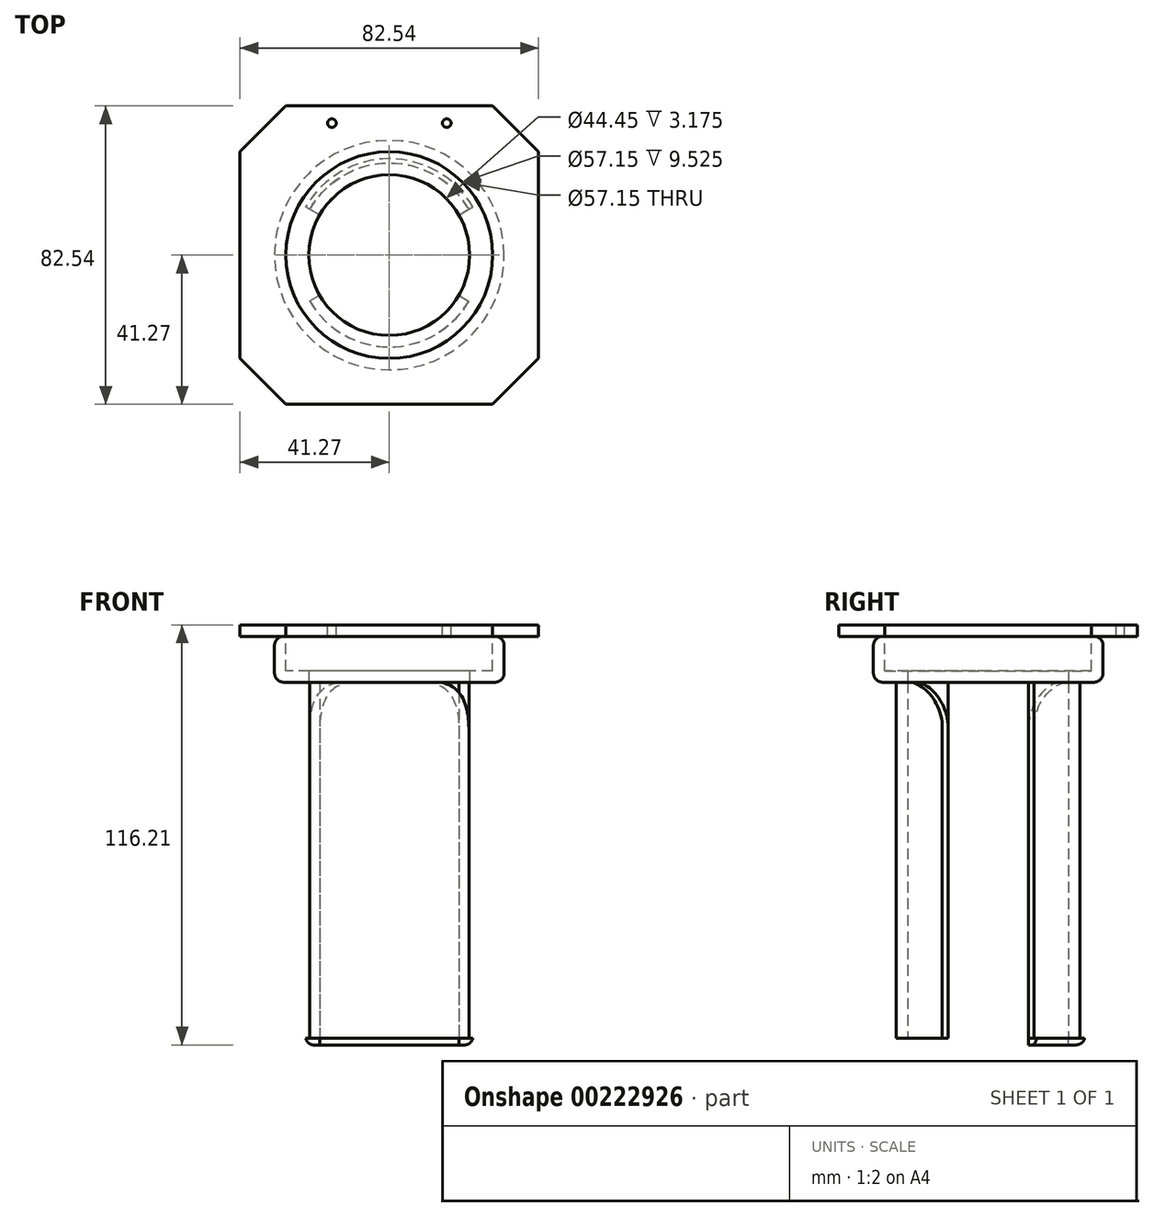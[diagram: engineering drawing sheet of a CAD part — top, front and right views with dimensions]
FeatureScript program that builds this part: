
annotation { "Feature Type Name" : "Feature", "Feature Type Description" : "" }
export const myFeature = defineFeature(function(context is Context, id is Id, definition is map)
    precondition{}
    {
        {
            var Q0;
            Q0=qCreatedBy(makeId("Top.planeOp"),FACE);
            var sketch = newSketch(context, id + "F0", { "sketchPlane" : qUnion([Q0])});
            skCircle(sketch, "E0", {"center": v(0, 0) * mm, "radius": 25.4 * mm});
            skCircle(sketch, "E1", {"center": v(0, 0) * mm, "radius": 22.23 * mm});
            skLineSegment(sketch, "E2", {"start": v(-12.7, 22) * mm, "end": v(12.7, -22) * mm});
            skLineSegment(sketch, "E3", {"start": v(12.7, 22) * mm, "end": v(-12.7, -22) * mm});
            skSolve(sketch);
        }
        {
            var Q0;
            {var subQ0=sQuery(id+"F0.wireOp",EDGE,"E2");var subQ1=sQuery(id+"F0.wireOp",EDGE,"E0");var subQ2=makeQuery(id+"F0.imprint","INTERSECT",VERTEX,{"disambiguationData":[OD(0.0)],"derivedFrom":[subQ1,subQ0]});Q0=makeQuery(id+"F0.imprint","IMPRINT",FACE,{"disambiguationData":[TD([[makeQuery(id+"F0.imprint","IMPRINT",EDGE,{"disambiguationData":[TD([[subQ2,-1.0]])],"derivedFrom":subQ1}),1.0]])]});}
            var Q1;
            {var subQ0=sQuery(id+"F0.wireOp",EDGE,"E2");var subQ1=sQuery(id+"F0.wireOp",EDGE,"E0");var subQ2=makeQuery(id+"F0.imprint","INTERSECT",VERTEX,{"disambiguationData":[OD(1.0)],"derivedFrom":[subQ1,subQ0]});Q1=makeQuery(id+"F0.imprint","IMPRINT",FACE,{"disambiguationData":[TD([[makeQuery(id+"F0.imprint","IMPRINT",EDGE,{"disambiguationData":[TD([[subQ2,-1.0]])],"derivedFrom":subQ1}),1.0]])]});}
            extrude(context, id + "F1", {"entities" : qUnion([Q0, Q1]), "depth" : 98.42 * mm});
        }
        {
            var Q0;
            {var subQ0=sQuery(id+"F0.wireOp",EDGE,"E3");var subQ1=sQuery(id+"F0.wireOp",EDGE,"E0");var subQ2=makeQuery(id+"F0.imprint","INTERSECT",VERTEX,{"disambiguationData":[OD(1.0)],"derivedFrom":[subQ1,subQ0]});var subQ3=sQuery(id+"F0.wireOp",EDGE,"E1");var subQ5=sQuery(id+"F0.wireOp",EDGE,"E2");var subQ6=makeQuery(id+"F0.imprint","INTERSECT",VERTEX,{"disambiguationData":[OD(0.0)],"derivedFrom":[subQ1,subQ5]});var subQ7=makeQuery(id+"F0.imprint","INTERSECT",VERTEX,{"disambiguationData":[OD(0.0)],"derivedFrom":[subQ3,subQ5]});Q0=makeQuery(id+"F1.opExtrude","CAP_FACE",FACE,{"disambiguationData":[OSD([subQ1,subQ3,subQ5,subQ0]),TDD([makeQuery(id+"F0.imprint","IMPRINT",EDGE,{"disambiguationData":[TD([[subQ6,-1.0]])],"derivedFrom":subQ1}),makeQuery(id+"F0.imprint","IMPRINT",EDGE,{"disambiguationData":[TD([[subQ7,-1.0]])],"derivedFrom":subQ3}),makeQuery(id+"F0.imprint","IMPRINT",EDGE,{"disambiguationData":[TD([[subQ6,-1.0]])],"derivedFrom":subQ5}),makeQuery(id+"F0.imprint","IMPRINT",EDGE,{"disambiguationData":[TD([[subQ2,1.0]])],"derivedFrom":subQ0})])],"isStart":true});}
            var sketch = newSketch(context, id + "F2", { "sketchPlane" : qUnion([Q0])});
            skCircle(sketch, "E4", {"center": v(0, 0) * mm, "radius": 26.67 * mm});
            skCircle(sketch, "E5", {"center": v(0, 0) * mm, "radius": 22.23 * mm});
            skLineSegment(sketch, "E6", {"start": v(11.11, -19.25) * mm, "end": v(13.34, -23.1) * mm});
            skLineSegment(sketch, "E7", {"start": v(-11.11, -19.25) * mm, "end": v(-13.34, -23.1) * mm});
            skLineSegment(sketch, "E8", {"start": v(-11.11, 19.25) * mm, "end": v(-13.33, 23.1) * mm});
            skLineSegment(sketch, "E9", {"start": v(11.11, 19.25) * mm, "end": v(13.33, 23.1) * mm});
            skSolve(sketch);
        }
        {
            var Q0;
            {var subQ5=sQuery(id+"F0.wireOp",EDGE,"E0");var subQ6=makeQuery(id+"F1.opExtrude","CAP_EDGE",EDGE,{"disambiguationData":[OSD([subQ5]),TDD([makeQuery(id+"F0.imprint","IMPRINT",EDGE,{"disambiguationData":[TD([[makeQuery(id+"F0.imprint","INTERSECT",VERTEX,{"disambiguationData":[OD(0.0)],"derivedFrom":[subQ5,sQuery(id+"F0.wireOp",EDGE,"E2")]}),-1.0]])],"derivedFrom":subQ5})])],"isStart":true});Q0=makeQuery(id+"F2.imprint","IMPRINT",FACE,{"disambiguationData":[TD([[makeQuery(id+"F2.imprint","IMPRINT",EDGE,{"derivedFrom":subQ6}),1.0]])]});}
            var Q1;
            {var subQ0=sQuery(id+"F2.wireOp",EDGE,"E6");Q1=makeQuery(id+"F2.imprint","IMPRINT",FACE,{"disambiguationData":[TD([[makeQuery(id+"F2.imprint","IMPRINT",EDGE,{"derivedFrom":subQ0}),1.0]])]});}
            var Q2;
            {var subQ5=sQuery(id+"F0.wireOp",EDGE,"E0");var subQ6=makeQuery(id+"F1.opExtrude","CAP_EDGE",EDGE,{"disambiguationData":[OSD([subQ5]),TDD([makeQuery(id+"F0.imprint","IMPRINT",EDGE,{"disambiguationData":[TD([[makeQuery(id+"F0.imprint","INTERSECT",VERTEX,{"disambiguationData":[OD(0.0)],"derivedFrom":[subQ5,sQuery(id+"F0.wireOp",EDGE,"E2")]}),-1.0]])],"derivedFrom":subQ5})])],"isStart":true});Q2=makeQuery(id+"F2.imprint","IMPRINT",FACE,{"disambiguationData":[TD([[makeQuery(id+"F2.imprint","IMPRINT",EDGE,{"derivedFrom":subQ6}),-1.0]])]});}
            extrude(context, id + "F3", {"entities" : qUnion([Q0, Q1, Q2]), "depth" : 1.9 * mm});
        }
        {
            var Q0;
            {var subQ0=sQuery(id+"F0.wireOp",EDGE,"E3");var subQ1=sQuery(id+"F0.wireOp",EDGE,"E0");var subQ2=makeQuery(id+"F0.imprint","INTERSECT",VERTEX,{"disambiguationData":[OD(1.0)],"derivedFrom":[subQ1,subQ0]});var subQ3=sQuery(id+"F0.wireOp",EDGE,"E1");var subQ5=sQuery(id+"F0.wireOp",EDGE,"E2");var subQ6=makeQuery(id+"F0.imprint","INTERSECT",VERTEX,{"disambiguationData":[OD(0.0)],"derivedFrom":[subQ1,subQ5]});var subQ7=makeQuery(id+"F0.imprint","INTERSECT",VERTEX,{"disambiguationData":[OD(0.0)],"derivedFrom":[subQ3,subQ5]});Q0=makeQuery(id+"F1.opExtrude","CAP_FACE",FACE,{"disambiguationData":[OSD([subQ1,subQ3,subQ5,subQ0]),TDD([makeQuery(id+"F0.imprint","IMPRINT",EDGE,{"disambiguationData":[TD([[subQ6,-1.0]])],"derivedFrom":subQ1}),makeQuery(id+"F0.imprint","IMPRINT",EDGE,{"disambiguationData":[TD([[subQ7,-1.0]])],"derivedFrom":subQ3}),makeQuery(id+"F0.imprint","IMPRINT",EDGE,{"disambiguationData":[TD([[subQ6,-1.0]])],"derivedFrom":subQ5}),makeQuery(id+"F0.imprint","IMPRINT",EDGE,{"disambiguationData":[TD([[subQ2,1.0]])],"derivedFrom":subQ0})])],"isStart":false});}
            var sketch = newSketch(context, id + "F4", { "sketchPlane" : qUnion([Q0])});
            skCircle(sketch, "E10", {"center": v(0, 0) * mm, "radius": 31.75 * mm});
            skSolve(sketch);
        }
        {
            var Q0;
            Q0 = qSketchRegion(id + "F4", true);
            extrude(context, id + "F5", {"entities" : qUnion([Q0]), "depth" : 12.7 * mm});
        }
        {
            var Q0;
            Q0=makeQuery(id+"F5.opExtrude","CAP_FACE",FACE,{"disambiguationData":[OSD([sQuery(id+"F4.wireOp",EDGE,"E10")])],"isStart":false});
            var sketch = newSketch(context, id + "F6", { "sketchPlane" : qUnion([Q0])});
            skLineSegment(sketch, "E11.bottom", {"start": v(41.27, 41.28) * mm, "end": v(-41.28, 41.28) * mm});
            skLineSegment(sketch, "E11.top", {"start": v(41.28, -41.28) * mm, "end": v(-41.27, -41.28) * mm});
            skLineSegment(sketch, "E11.left", {"start": v(41.27, 41.28) * mm, "end": v(41.28, -41.28) * mm});
            skLineSegment(sketch, "E11.right", {"start": v(-41.28, 41.28) * mm, "end": v(-41.27, -41.28) * mm});
            skPoint(sketch, "E11.middle", {"position": v(0, 0) * mm});
            skSolve(sketch);
        }
        {
            var Q0;
            Q0 = qSketchRegion(id + "F6", true);
            extrude(context, id + "F7", {"entities" : qUnion([Q0]), "depth" : 3.17 * mm});
        }
        {
            var Q0;
            Q0=makeQuery(id+"F7.opExtrude","CAP_FACE",FACE,{"disambiguationData":[OSD([sQuery(id+"F6.wireOp",EDGE,"E11.bottom"),sQuery(id+"F6.wireOp",EDGE,"E11.top"),sQuery(id+"F6.wireOp",EDGE,"E11.left"),sQuery(id+"F6.wireOp",EDGE,"E11.right")])],"isStart":false});
            var sketch = newSketch(context, id + "F8", { "sketchPlane" : qUnion([Q0])});
            skLineSegment(sketch, "E12.bottom", {"start": v(11.9, 38.1) * mm, "end": v(-11.9, 38.1) * mm});
            skLineSegment(sketch, "E12.top", {"start": v(11.9, 34.93) * mm, "end": v(-11.9, 34.93) * mm});
            skLineSegment(sketch, "E12.left", {"start": v(11.9, 38.1) * mm, "end": v(11.9, 34.93) * mm});
            skLineSegment(sketch, "E12.right", {"start": v(-11.9, 38.1) * mm, "end": v(-11.9, 34.93) * mm});
            skPoint(sketch, "E12.middle", {"position": v(0, 36.51) * mm});
            skCircle(sketch, "E13", {"center": v(-15.88, 36.51) * mm, "radius": 1.2 * mm});
            skCircle(sketch, "E14", {"center": v(15.88, 36.51) * mm, "radius": 1.2 * mm});
            skSolve(sketch);
        }
        {
            var Q0;
            {var subQ0=sQuery(id+"F0.wireOp",EDGE,"E3");var subQ1=sQuery(id+"F0.wireOp",EDGE,"E0");var subQ2=makeQuery(id+"F0.imprint","INTERSECT",VERTEX,{"disambiguationData":[OD(1.0)],"derivedFrom":[subQ1,subQ0]});var subQ3=sQuery(id+"F0.wireOp",EDGE,"E1");var subQ5=sQuery(id+"F0.wireOp",EDGE,"E2");var subQ6=makeQuery(id+"F0.imprint","INTERSECT",VERTEX,{"disambiguationData":[OD(0.0)],"derivedFrom":[subQ1,subQ5]});var subQ7=makeQuery(id+"F0.imprint","INTERSECT",VERTEX,{"disambiguationData":[OD(0.0)],"derivedFrom":[subQ3,subQ5]});Q0=makeQuery(id+"F1.opExtrude","SWEPT_BODY",BODY,{"disambiguationData":[OSD([subQ1,subQ3,subQ5,subQ0]),TDD([makeQuery(id+"F0.imprint","IMPRINT",EDGE,{"disambiguationData":[TD([[subQ6,-1.0]])],"derivedFrom":subQ1}),makeQuery(id+"F0.imprint","IMPRINT",EDGE,{"disambiguationData":[TD([[subQ7,-1.0]])],"derivedFrom":subQ3}),makeQuery(id+"F0.imprint","IMPRINT",EDGE,{"disambiguationData":[TD([[subQ6,-1.0]])],"derivedFrom":subQ5}),makeQuery(id+"F0.imprint","IMPRINT",EDGE,{"disambiguationData":[TD([[subQ2,1.0]])],"derivedFrom":subQ0})])]});}
            var Q1;
            {var subQ0=sQuery(id+"F0.wireOp",EDGE,"E3");var subQ1=sQuery(id+"F0.wireOp",EDGE,"E0");var subQ2=makeQuery(id+"F0.imprint","INTERSECT",VERTEX,{"disambiguationData":[OD(0.0)],"derivedFrom":[subQ1,subQ0]});var subQ3=sQuery(id+"F0.wireOp",EDGE,"E1");var subQ4=makeQuery(id+"F0.imprint","INTERSECT",VERTEX,{"disambiguationData":[OD(0.0)],"derivedFrom":[subQ3,subQ0]});var subQ5=sQuery(id+"F0.wireOp",EDGE,"E2");var subQ6=makeQuery(id+"F0.imprint","INTERSECT",VERTEX,{"disambiguationData":[OD(1.0)],"derivedFrom":[subQ1,subQ5]});Q1=makeQuery(id+"F1.opExtrude","SWEPT_BODY",BODY,{"disambiguationData":[OSD([subQ1,subQ3,subQ5,subQ0]),TDD([makeQuery(id+"F0.imprint","IMPRINT",EDGE,{"disambiguationData":[TD([[subQ6,-1.0]])],"derivedFrom":subQ1}),makeQuery(id+"F0.imprint","IMPRINT",EDGE,{"disambiguationData":[TD([[subQ4,1.0]])],"derivedFrom":subQ3}),makeQuery(id+"F0.imprint","IMPRINT",EDGE,{"disambiguationData":[TD([[subQ6,1.0]])],"derivedFrom":subQ5}),makeQuery(id+"F0.imprint","IMPRINT",EDGE,{"disambiguationData":[TD([[subQ2,-1.0]])],"derivedFrom":subQ0})])]});}
            var Q2;
            Q2=makeQuery(id+"F3.opExtrude","SWEPT_BODY",BODY,{"disambiguationData":[OSD([sQuery(id+"F2.wireOp",EDGE,"E4"),sQuery(id+"F2.wireOp",EDGE,"E5"),sQuery(id+"F2.wireOp",EDGE,"E7"),sQuery(id+"F2.wireOp",EDGE,"E8")])]});
            var Q3;
            Q3=makeQuery(id+"F3.opExtrude","SWEPT_BODY",BODY,{"disambiguationData":[OSD([sQuery(id+"F2.wireOp",EDGE,"E4"),sQuery(id+"F2.wireOp",EDGE,"E5"),sQuery(id+"F2.wireOp",EDGE,"E6"),sQuery(id+"F2.wireOp",EDGE,"E9")])]});
            var Q4;
            {var subQ0=sQuery(id+"F0.wireOp",EDGE,"E1");Q4=makeQuery(id+"F1.opExtrude","SWEPT_FACE",FACE,{"disambiguationData":[OSD([subQ0]),TDD([makeQuery(id+"F0.imprint","IMPRINT",EDGE,{"disambiguationData":[TD([[makeQuery(id+"F0.imprint","INTERSECT",VERTEX,{"disambiguationData":[OD(0.0)],"derivedFrom":[subQ0,sQuery(id+"F0.wireOp",EDGE,"E2")]}),-1.0]])],"derivedFrom":subQ0})])]});}
            transform(context, id + "F9", {"entities" : qUnion([Q0, Q1, Q2, Q3]), "transformType" : TransformType.ROTATION, "transformAxis" : qUnion([Q4]), "angle" : 90 * degree, "makeCopy" : false});
        }
        {
            var Q0;
            Q0=makeQuery(id+"F5.opExtrude","CAP_FACE",FACE,{"disambiguationData":[OSD([sQuery(id+"F4.wireOp",EDGE,"E10")])],"isStart":true});
            var sketch = newSketch(context, id + "F10", { "sketchPlane" : qUnion([Q0])});
            skCircle(sketch, "E15", {"center": v(0, 0) * mm, "radius": 22.23 * mm});
            skSolve(sketch);
        }
        {
            var Q0;
            Q0 = qSketchRegion(id + "F10", true);
            extrude(context, id + "F11", {"entities" : qUnion([Q0]), "operationType" : NewBodyOperationType.REMOVE, "oppositeDirection" : true, "depth" : 76.2 * mm});
        }
        {
            var Q0;
            Q0=makeQuery(id+"F7.opExtrude","CAP_FACE",FACE,{"disambiguationData":[OSD([sQuery(id+"F6.wireOp",EDGE,"E11.bottom"),sQuery(id+"F6.wireOp",EDGE,"E11.top"),sQuery(id+"F6.wireOp",EDGE,"E11.left"),sQuery(id+"F6.wireOp",EDGE,"E11.right")])],"isStart":false});
            var sketch = newSketch(context, id + "F12", { "sketchPlane" : qUnion([Q0])});
            skCircle(sketch, "E16", {"center": v(0, 0) * mm, "radius": 28.58 * mm});
            skSolve(sketch);
        }
        {
            var Q0;
            Q0 = qSketchRegion(id + "F12", true);
            extrude(context, id + "F13", {"entities" : qUnion([Q0]), "operationType" : NewBodyOperationType.REMOVE, "oppositeDirection" : true, "depth" : 12.7 * mm});
        }
        {
            var Q0;
            Q0=makeQuery(id+"FxAJugrmvYLoY7f_6.opExtrude","SWEPT_EDGE",EDGE,{"disambiguationData":[OSD([sQuery(id+"Fw4iDfrlL6vGLhg_6.wireOp",EDGE,"gR0BklfV-5mPJ-LLUH-3pZj-btvfWRUNL7RN.bottom"),sQuery(id+"Fw4iDfrlL6vGLhg_6.wireOp",EDGE,"gR0BklfV-5mPJ-LLUH-3pZj-btvfWRUNL7RN.left")])]});
            var Q1;
            Q1=makeQuery(id+"FxAJugrmvYLoY7f_6.opExtrude","SWEPT_EDGE",EDGE,{"disambiguationData":[OSD([sQuery(id+"Fw4iDfrlL6vGLhg_6.wireOp",EDGE,"gR0BklfV-5mPJ-LLUH-3pZj-btvfWRUNL7RN.bottom"),sQuery(id+"Fw4iDfrlL6vGLhg_6.wireOp",EDGE,"gR0BklfV-5mPJ-LLUH-3pZj-btvfWRUNL7RN.right")])]});
            var Q2;
            Q2=makeQuery(id+"F7.opExtrude","SWEPT_EDGE",EDGE,{"disambiguationData":[OSD([sQuery(id+"F6.wireOp",EDGE,"E11.bottom"),sQuery(id+"F6.wireOp",EDGE,"E11.right")])]});
            var Q3;
            Q3=makeQuery(id+"F7.opExtrude","SWEPT_EDGE",EDGE,{"disambiguationData":[OSD([sQuery(id+"F6.wireOp",EDGE,"E11.bottom"),sQuery(id+"F6.wireOp",EDGE,"E11.left")])]});
            var Q4;
            Q4=makeQuery(id+"F7.opExtrude","SWEPT_EDGE",EDGE,{"disambiguationData":[OSD([sQuery(id+"F6.wireOp",EDGE,"E11.top"),sQuery(id+"F6.wireOp",EDGE,"E11.right")])]});
            var Q5;
            Q5=makeQuery(id+"F7.opExtrude","SWEPT_EDGE",EDGE,{"disambiguationData":[OSD([sQuery(id+"F6.wireOp",EDGE,"E11.top"),sQuery(id+"F6.wireOp",EDGE,"E11.left")])]});
            var Q6;
            Q6=makeQuery(id+"FxAJugrmvYLoY7f_6.opExtrude","SWEPT_EDGE",EDGE,{"disambiguationData":[OSD([sQuery(id+"Fw4iDfrlL6vGLhg_6.wireOp",EDGE,"gR0BklfV-5mPJ-LLUH-3pZj-btvfWRUNL7RN.top"),sQuery(id+"Fw4iDfrlL6vGLhg_6.wireOp",EDGE,"gR0BklfV-5mPJ-LLUH-3pZj-btvfWRUNL7RN.right")])]});
            var Q7;
            Q7=makeQuery(id+"FxAJugrmvYLoY7f_6.opExtrude","SWEPT_EDGE",EDGE,{"disambiguationData":[OSD([sQuery(id+"Fw4iDfrlL6vGLhg_6.wireOp",EDGE,"gR0BklfV-5mPJ-LLUH-3pZj-btvfWRUNL7RN.top"),sQuery(id+"Fw4iDfrlL6vGLhg_6.wireOp",EDGE,"gR0BklfV-5mPJ-LLUH-3pZj-btvfWRUNL7RN.left")])]});
            chamfer(context, id + "F14", {"entities" : qUnion([Q0, Q1, Q2, Q3, Q4, Q5, Q6, Q7]), "width" : 12.7 * mm, "tangentPropagation" : true});
        }
        {
            var Q0;
            {var subQ0=sQuery(id+"F2.wireOp",EDGE,"E4");Q0=makeQuery(id+"F3.opExtrude","CAP_EDGE",EDGE,{"disambiguationData":[OSD([subQ0]),TDD([makeQuery(id+"F2.imprint","IMPRINT",EDGE,{"disambiguationData":[TD([[makeQuery(id+"F2.imprint","INTERSECT",VERTEX,{"derivedFrom":[subQ0,sQuery(id+"F2.wireOp",EDGE,"E6")]}),-1.0]])],"derivedFrom":subQ0})])],"isStart":false});}
            var Q1;
            {var subQ0=sQuery(id+"F2.wireOp",EDGE,"E4");Q1=makeQuery(id+"F3.opExtrude","CAP_EDGE",EDGE,{"disambiguationData":[OSD([subQ0]),TDD([makeQuery(id+"F2.imprint","IMPRINT",EDGE,{"disambiguationData":[TD([[makeQuery(id+"F2.imprint","INTERSECT",VERTEX,{"derivedFrom":[subQ0,sQuery(id+"F2.wireOp",EDGE,"E7")]}),1.0]])],"derivedFrom":subQ0})])],"isStart":false});}
            fillet(context, id + "F15", {"entities" : qUnion([Q0, Q1]), "radius" : 2.54 * mm, "tangentPropagation" : true, "allowEdgeOverflow" : false});
        }
        {
            var Q0;
            {var subQ0=sQuery(id+"F0.wireOp",EDGE,"E3");Q0=makeQuery(id+"F1.opExtrude","CAP_EDGE",EDGE,{"disambiguationData":[OSD([subQ0]),TDD([makeQuery(id+"F0.imprint","IMPRINT",EDGE,{"disambiguationData":[TD([[makeQuery(id+"F0.imprint","INTERSECT",VERTEX,{"disambiguationData":[OD(1.0)],"derivedFrom":[sQuery(id+"F0.wireOp",EDGE,"E0"),subQ0]}),1.0]])],"derivedFrom":subQ0})])],"isStart":false});}
            var Q1;
            {var subQ0=sQuery(id+"F0.wireOp",EDGE,"E2");Q1=makeQuery(id+"F1.opExtrude","CAP_EDGE",EDGE,{"disambiguationData":[OSD([subQ0]),TDD([makeQuery(id+"F0.imprint","IMPRINT",EDGE,{"disambiguationData":[TD([[makeQuery(id+"F0.imprint","INTERSECT",VERTEX,{"disambiguationData":[OD(1.0)],"derivedFrom":[sQuery(id+"F0.wireOp",EDGE,"E0"),subQ0]}),1.0]])],"derivedFrom":subQ0})])],"isStart":false});}
            var Q2;
            {var subQ0=sQuery(id+"F0.wireOp",EDGE,"E3");Q2=makeQuery(id+"F1.opExtrude","CAP_EDGE",EDGE,{"disambiguationData":[OSD([subQ0]),TDD([makeQuery(id+"F0.imprint","IMPRINT",EDGE,{"disambiguationData":[TD([[makeQuery(id+"F0.imprint","INTERSECT",VERTEX,{"disambiguationData":[OD(0.0)],"derivedFrom":[sQuery(id+"F0.wireOp",EDGE,"E0"),subQ0]}),-1.0]])],"derivedFrom":subQ0})])],"isStart":false});}
            var Q3;
            {var subQ0=sQuery(id+"F0.wireOp",EDGE,"E2");Q3=makeQuery(id+"F1.opExtrude","CAP_EDGE",EDGE,{"disambiguationData":[OSD([subQ0]),TDD([makeQuery(id+"F0.imprint","IMPRINT",EDGE,{"disambiguationData":[TD([[makeQuery(id+"F0.imprint","INTERSECT",VERTEX,{"disambiguationData":[OD(0.0)],"derivedFrom":[sQuery(id+"F0.wireOp",EDGE,"E0"),subQ0]}),-1.0]])],"derivedFrom":subQ0})])],"isStart":false});}
            fillet(context, id + "F16", {"entities" : qUnion([Q0, Q1, Q2, Q3]), "radius" : 12.7 * mm, "tangentPropagation" : true, "allowEdgeOverflow" : false});
        }
        {
            var Q0;
            Q0=makeQuery(id+"F5.opExtrude","CAP_EDGE",EDGE,{"disambiguationData":[OSD([sQuery(id+"F4.wireOp",EDGE,"E10")])],"isStart":true});
            var Q1;
            Q1=makeQuery(id+"F5.opExtrude","CAP_EDGE",EDGE,{"disambiguationData":[OSD([sQuery(id+"F4.wireOp",EDGE,"E10")])],"isStart":false});
            fillet(context, id + "F17", {"entities" : qUnion([Q0, Q1]), "radius" : 2.54 * mm, "tangentPropagation" : true, "allowEdgeOverflow" : false});
        }
        {
            var Q0;
            Q0=makeQuery(id+"F8.imprint","IMPRINT",FACE,{"disambiguationData":[TD([[makeQuery(id+"F8.imprint","IMPRINT",EDGE,{"derivedFrom":sQuery(id+"F8.wireOp",EDGE,"E13")}),1.0]])]});
            var Q1;
            Q1=makeQuery(id+"F8.imprint","IMPRINT",FACE,{"disambiguationData":[TD([[makeQuery(id+"F8.imprint","IMPRINT",EDGE,{"derivedFrom":sQuery(id+"F8.wireOp",EDGE,"E14")}),1.0]])]});
            extrude(context, id + "F18", {"entities" : qUnion([Q0, Q1]), "operationType" : NewBodyOperationType.REMOVE, "oppositeDirection" : true, "depth" : 25.4 * mm});
        }
    });
